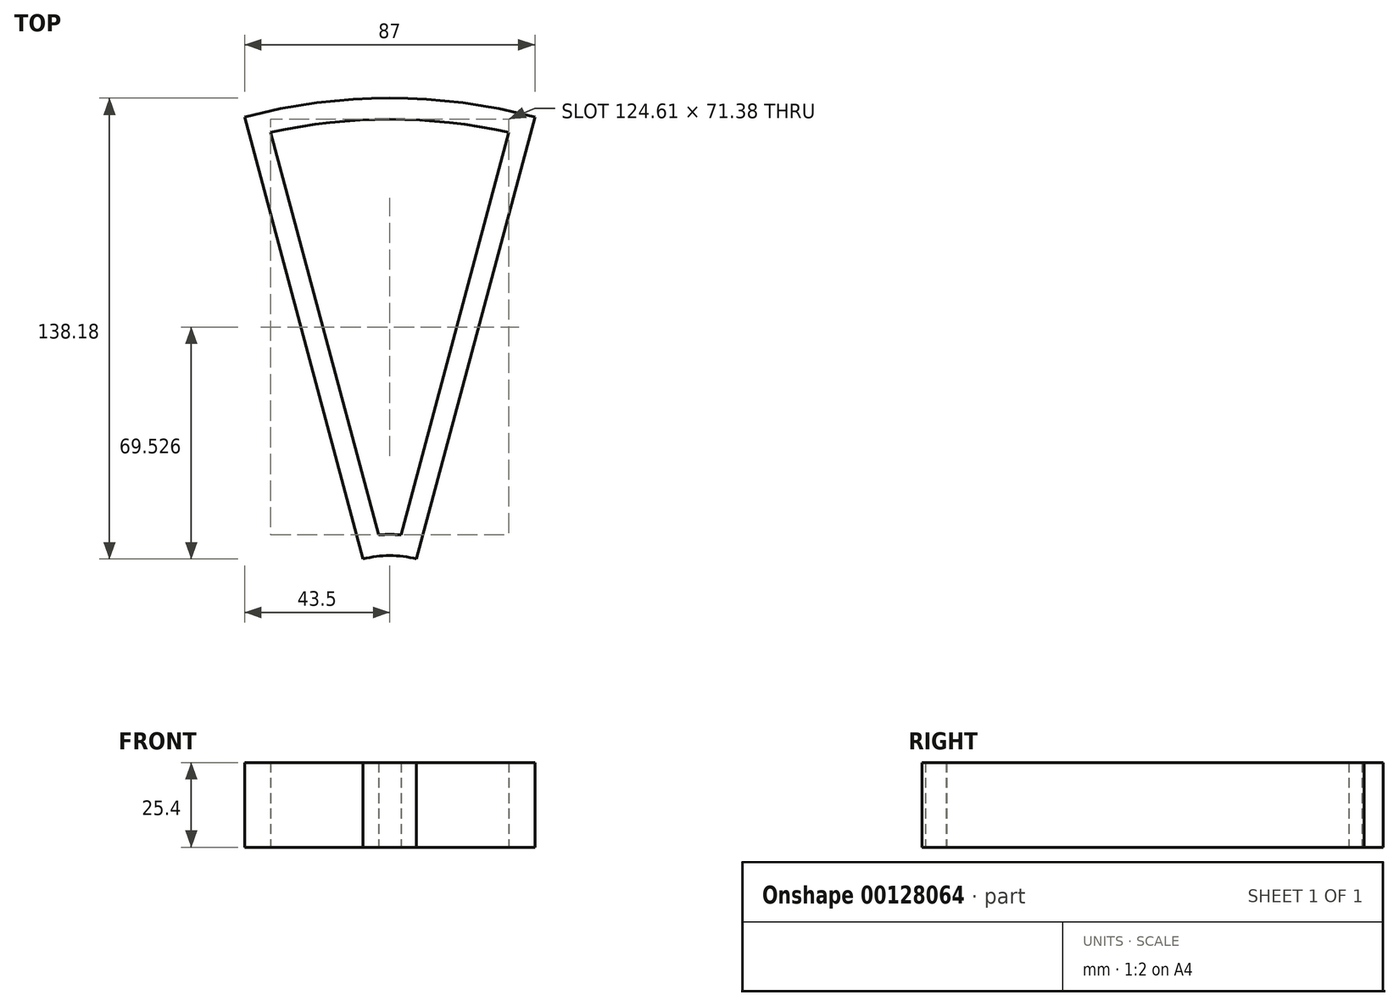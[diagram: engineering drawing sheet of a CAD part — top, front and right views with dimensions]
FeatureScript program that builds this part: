
annotation { "Feature Type Name" : "Feature", "Feature Type Description" : "" }
export const myFeature = defineFeature(function(context is Context, id is Id, definition is map)
    precondition{}
    {
        {
            var Q0;
            Q0=qCreatedBy(makeId("Top.planeOp"),FACE);
            var sketch = newSketch(context, id + "F0", { "sketchPlane" : qUnion([Q0])});
            skArc(sketch, "E0", {"start": v(8, 30.73) * mm, "mid": v(0, 31.75) * mm, "end": v(-8, 30.73) * mm});
            skArc(sketch, "E1", {"start": v(43.5, 163.21) * mm, "mid": v(0, 168.91) * mm, "end": v(-43.5, 163.21) * mm});
            skLineSegment(sketch, "E2", {"start": v(8, 30.73) * mm, "end": v(43.5, 163.21) * mm});
            skLineSegment(sketch, "E3", {"start": v(-43.5, 163.21) * mm, "end": v(-8, 30.73) * mm});
            skLineSegment(sketch, "E4", {"start": v(0, 0) * mm, "end": v(0, 96.4) * mm, "construction": true});
            skLineSegment(sketch, "E5", {"start": v(3.36, 37.95) * mm, "end": v(35.69, 158.6) * mm});
            skLineSegment(sketch, "E6", {"start": v(-35.69, 158.6) * mm, "end": v(-3.36, 37.95) * mm});
            skArc(sketch, "E7", {"start": v(-3.36, 37.95) * mm, "mid": v(0, 38.1) * mm, "end": v(3.36, 37.95) * mm});
            skArc(sketch, "E8", {"start": v(35.69, 158.6) * mm, "mid": v(0, 162.56) * mm, "end": v(-35.69, 158.6) * mm});
            skSolve(sketch);
        }
        {
            var Q0;
            Q0=makeQuery(id+"F0.imprint","IMPRINT",FACE,{"disambiguationData":[TD([[makeQuery(id+"F0.imprint","IMPRINT",EDGE,{"derivedFrom":sQuery(id+"F0.wireOp",EDGE,"E0")}),-1.0]])]});
            extrude(context, id + "F1", {"entities" : qUnion([Q0]), "depth" : 25.4 * mm});
        }
    });
